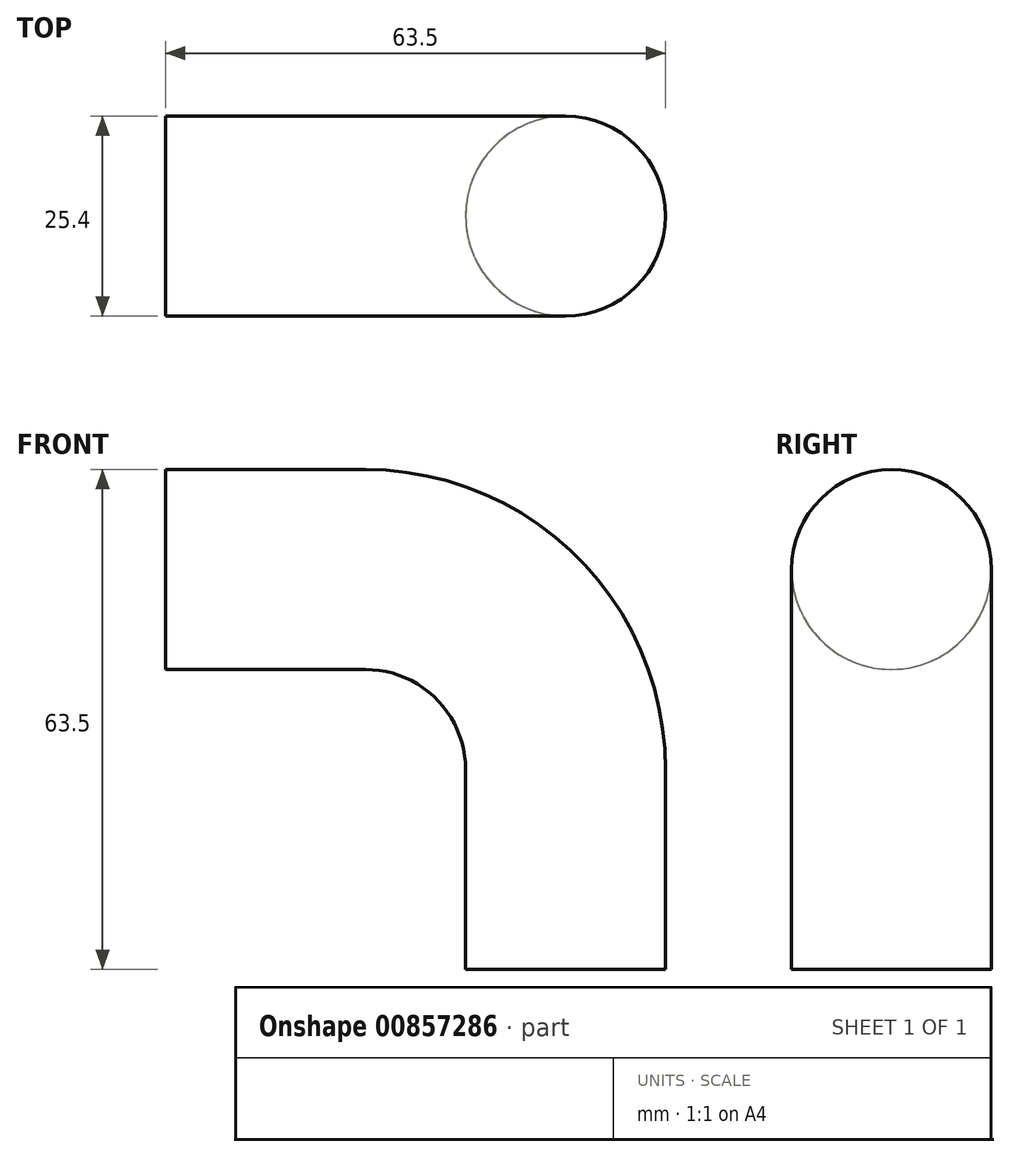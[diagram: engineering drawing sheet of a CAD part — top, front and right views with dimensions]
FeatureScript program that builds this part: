
annotation { "Feature Type Name" : "Feature", "Feature Type Description" : "" }
export const myFeature = defineFeature(function(context is Context, id is Id, definition is map)
    precondition{}
    {
        {
            var Q0;
            Q0=qCreatedBy(makeId("Front.planeOp"),FACE);
            var sketch = newSketch(context, id + "F0", { "sketchPlane" : qUnion([Q0])});
            skLineSegment(sketch, "E0", {"start": v(0, 0) * mm, "end": v(0, 25.4) * mm});
            skLineSegment(sketch, "E1", {"start": v(-25.4, 50.8) * mm, "end": v(-50.8, 50.8) * mm});
            skPoint(sketch, "E2.visualSharp", {"position": v(0, 50.8) * mm});
            skArc(sketch, "E2.filletArc", {"start": v(0, 25.4) * mm, "mid": v(-7.44, 43.36) * mm, "end": v(-25.4, 50.8) * mm});
            skSolve(sketch);
        }
        {
            var Q0;
            Q0=qCreatedBy(makeId("Top.planeOp"),FACE);
            var sketch = newSketch(context, id + "F1", { "sketchPlane" : qUnion([Q0])});
            skCircle(sketch, "E3", {"center": v(0, 0) * mm, "radius": 12.7 * mm});
            skSolve(sketch);
        }
        {
            var Q0;
            Q0=makeQuery(id+"F1.imprint","IMPRINT",FACE,{"disambiguationData":[TD([[makeQuery(id+"F1.imprint","IMPRINT",EDGE,{"derivedFrom":sQuery(id+"F1.wireOp",EDGE,"E3")}),1.0]])]});
            var Q1;
            Q1=sQuery(id+"F0.wireOp",EDGE,"E0");
            var Q2;
            Q2=sQuery(id+"F0.wireOp",EDGE,"E2.filletArc");
            var Q3;
            Q3=sQuery(id+"F0.wireOp",EDGE,"E1");
            sweep(context, id + "F2", {"profiles" : qUnion([Q0]), "path" : qUnion([Q1, Q2, Q3])});
        }
    });
